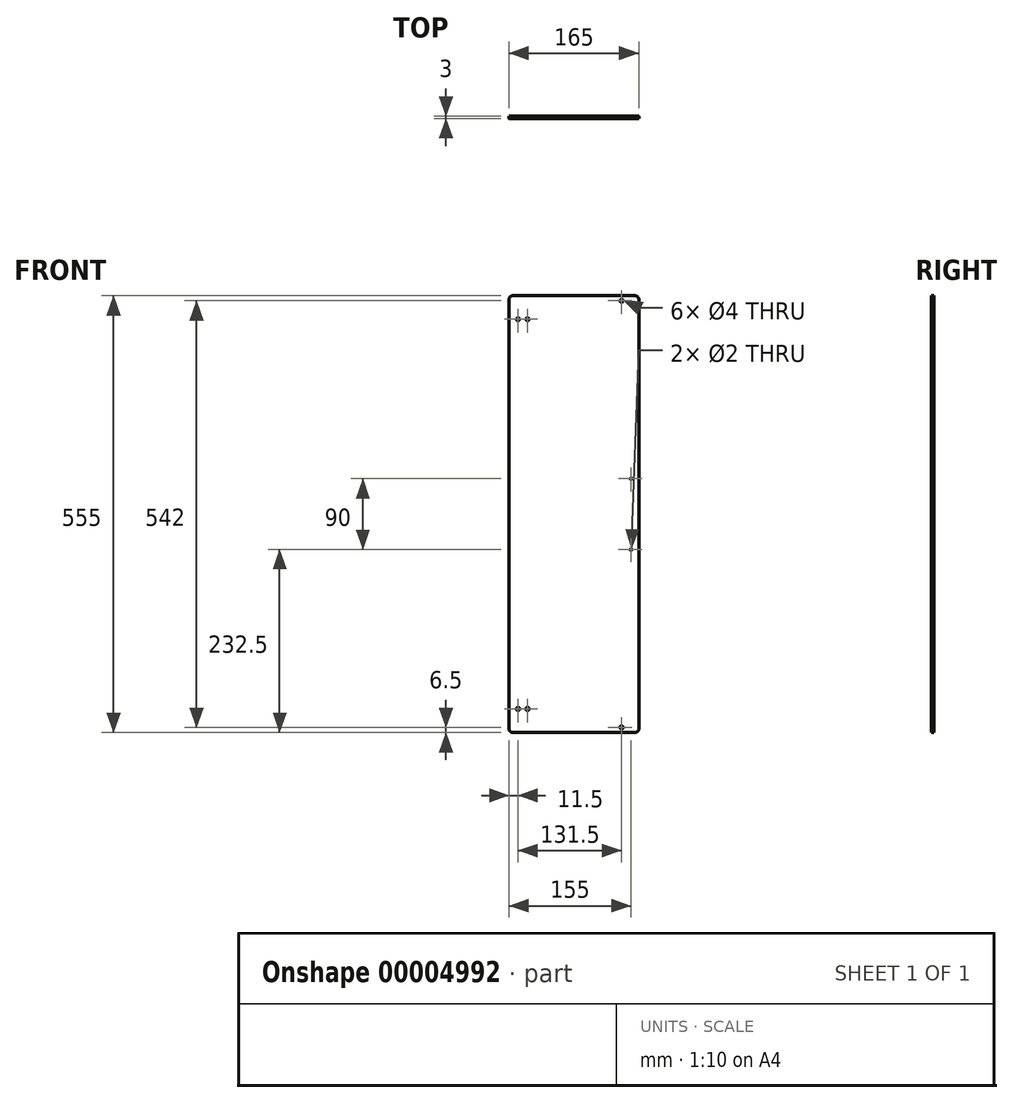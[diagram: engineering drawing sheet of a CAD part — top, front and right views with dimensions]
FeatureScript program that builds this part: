
annotation { "Feature Type Name" : "Feature", "Feature Type Description" : "" }
export const myFeature = defineFeature(function(context is Context, id is Id, definition is map)
    precondition{}
    {
        {
            var Q0;
            Q0=qCreatedBy(makeId("Front.planeOp"),FACE);
            var sketch = newSketch(context, id + "F0", { "sketchPlane" : qUnion([Q0])});
            skLineSegment(sketch, "E0.rect.bottom", {"start": v(82.5, 277.5) * mm, "end": v(-82.5, 277.5) * mm});
            skLineSegment(sketch, "E0.rect.top", {"start": v(82.5, -277.5) * mm, "end": v(-82.5, -277.5) * mm});
            skLineSegment(sketch, "E0.rect.left", {"start": v(82.5, 277.5) * mm, "end": v(82.5, -277.5) * mm});
            skLineSegment(sketch, "E0.rect.right", {"start": v(-82.5, 277.5) * mm, "end": v(-82.5, -277.5) * mm});
            skPoint(sketch, "E0.rect.middle", {"position": v(0, 0) * mm});
            skLineSegment(sketch, "E1", {"start": v(0, 277.5) * mm, "end": v(0, -277.5) * mm, "construction": true});
            skLineSegment(sketch, "E2", {"start": v(0, 0) * mm, "end": v(82.5, 0) * mm, "construction": true});
            skCircle(sketch, "E3", {"center": v(80.17, 273.25) * mm, "radius": 1.5 * mm, "construction": true});
            skCircle(sketch, "E4.0.MirrorC", {"center": v(80.17, -273.25) * mm, "radius": 1.5 * mm, "construction": true});
            skCircle(sketch, "E5.0.MirrorC", {"center": v(-80.17, -273.25) * mm, "radius": 1.5 * mm, "construction": true});
            skCircle(sketch, "E5.1.MirrorC", {"center": v(-80.17, 273.25) * mm, "radius": 1.5 * mm, "construction": true});
            skSolve(sketch);
        }
        {
            var Q0;
            Q0=qSketchRegion(id+"F0",true);
            extrude(context, id + "F1", {"entities" : qUnion([Q0]), "depth" : 3 * mm});
        }
        {
            var Q0;
            Q0=makeQuery(id+"F1.opExtrude","SWEPT_EDGE",EDGE,{"disambiguationData":[OSD([sQuery(id+"F0.wireOp",EDGE,"E0.rect.bottom"),sQuery(id+"F0.wireOp",EDGE,"E0.rect.left")])]});
            var Q1;
            Q1=makeQuery(id+"F1.opExtrude","SWEPT_EDGE",EDGE,{"disambiguationData":[OSD([sQuery(id+"F0.wireOp",EDGE,"E0.rect.bottom"),sQuery(id+"F0.wireOp",EDGE,"E0.rect.right")])]});
            var Q2;
            Q2=makeQuery(id+"F1.opExtrude","SWEPT_EDGE",EDGE,{"disambiguationData":[OSD([sQuery(id+"F0.wireOp",EDGE,"E0.rect.top"),sQuery(id+"F0.wireOp",EDGE,"E0.rect.left")])]});
            var Q3;
            Q3=makeQuery(id+"F1.opExtrude","SWEPT_EDGE",EDGE,{"disambiguationData":[OSD([sQuery(id+"F0.wireOp",EDGE,"E0.rect.top"),sQuery(id+"F0.wireOp",EDGE,"E0.rect.right")])]});
            fillet(context, id + "F2", {"entities" : qUnion([Q0, Q1, Q2, Q3]), "radius" : 5 * mm, "tangentPropagation" : true, "allowEdgeOverflow" : false});
        }
        {
            var Q0;
            Q0=makeQuery(id+"F1.opExtrude","CAP_FACE",FACE,{"disambiguationData":[OSD([sQuery(id+"F0.wireOp",EDGE,"E0.rect.bottom"),sQuery(id+"F0.wireOp",EDGE,"E0.rect.top"),sQuery(id+"F0.wireOp",EDGE,"E0.rect.left"),sQuery(id+"F0.wireOp",EDGE,"E0.rect.right")])],"isStart":false});
            var sketch = newSketch(context, id + "F3", { "sketchPlane" : qUnion([Q0])});
            skLineSegment(sketch, "E6", {"start": v(-82.5, 0) * mm, "end": v(82.5, 0) * mm, "construction": true});
            skLineSegment(sketch, "E7", {"start": v(-82.5, 247.5) * mm, "end": v(82.5, 247.5) * mm, "construction": true});
            skCircle(sketch, "E8", {"center": v(-71, 247.5) * mm, "radius": 2 * mm});
            skCircle(sketch, "E9", {"center": v(-59, 247.5) * mm, "radius": 2 * mm});
            skCircle(sketch, "E10.0.MirrorC", {"center": v(-59, -247.5) * mm, "radius": 2 * mm});
            skCircle(sketch, "E10.1.MirrorC", {"center": v(-71, -247.5) * mm, "radius": 2 * mm});
            skSolve(sketch);
        }
        {
            var Q0;
            Q0 = qSketchRegion(id + "F3", true);
            extrude(context, id + "F4", {"entities" : qUnion([Q0]), "operationType" : NewBodyOperationType.REMOVE, "endBound" : BoundingType.THROUGH_ALL, "oppositeDirection" : true, "depth" : 25 * mm});
        }
        {
            var Q0;
            Q0=makeQuery(id+"F1.opExtrude","CAP_FACE",FACE,{"disambiguationData":[OSD([sQuery(id+"F0.wireOp",EDGE,"E0.rect.bottom"),sQuery(id+"F0.wireOp",EDGE,"E0.rect.top"),sQuery(id+"F0.wireOp",EDGE,"E0.rect.left"),sQuery(id+"F0.wireOp",EDGE,"E0.rect.right")])],"isStart":false});
            var sketch = newSketch(context, id + "F5", { "sketchPlane" : qUnion([Q0])});
            skCircle(sketch, "E11", {"center": v(60.5, 271) * mm, "radius": 2 * mm});
            skLineSegment(sketch, "E12", {"start": v(0, 0) * mm, "end": v(139.05, 0) * mm, "construction": true});
            skCircle(sketch, "E13.0.MirrorC", {"center": v(60.5, -271) * mm, "radius": 2 * mm});
            skSolve(sketch);
        }
        {
            var Q0;
            Q0 = qSketchRegion(id + "F5", true);
            extrude(context, id + "F6", {"entities" : qUnion([Q0]), "operationType" : NewBodyOperationType.REMOVE, "endBound" : BoundingType.THROUGH_ALL, "oppositeDirection" : true, "depth" : 25 * mm});
        }
        {
            var Q0;
            Q0=makeQuery(id+"F1.opExtrude","CAP_FACE",FACE,{"disambiguationData":[OSD([sQuery(id+"F0.wireOp",EDGE,"E0.rect.bottom"),sQuery(id+"F0.wireOp",EDGE,"E0.rect.top"),sQuery(id+"F0.wireOp",EDGE,"E0.rect.left"),sQuery(id+"F0.wireOp",EDGE,"E0.rect.right")])],"isStart":false});
            var sketch = newSketch(context, id + "F7", { "sketchPlane" : qUnion([Q0])});
            skLineSegment(sketch, "E14", {"start": v(0, 0) * mm, "end": v(84.02, 0) * mm, "construction": true});
            skCircle(sketch, "E15", {"center": v(72.5, 45) * mm, "radius": 1 * mm});
            skCircle(sketch, "E16.0.MirrorC", {"center": v(72.5, -45) * mm, "radius": 1 * mm});
            skSolve(sketch);
        }
        {
            var Q0;
            Q0 = qSketchRegion(id + "F7", true);
            extrude(context, id + "F8", {"entities" : qUnion([Q0]), "operationType" : NewBodyOperationType.REMOVE, "endBound" : BoundingType.THROUGH_ALL, "oppositeDirection" : true, "depth" : 25 * mm});
        }
    });
